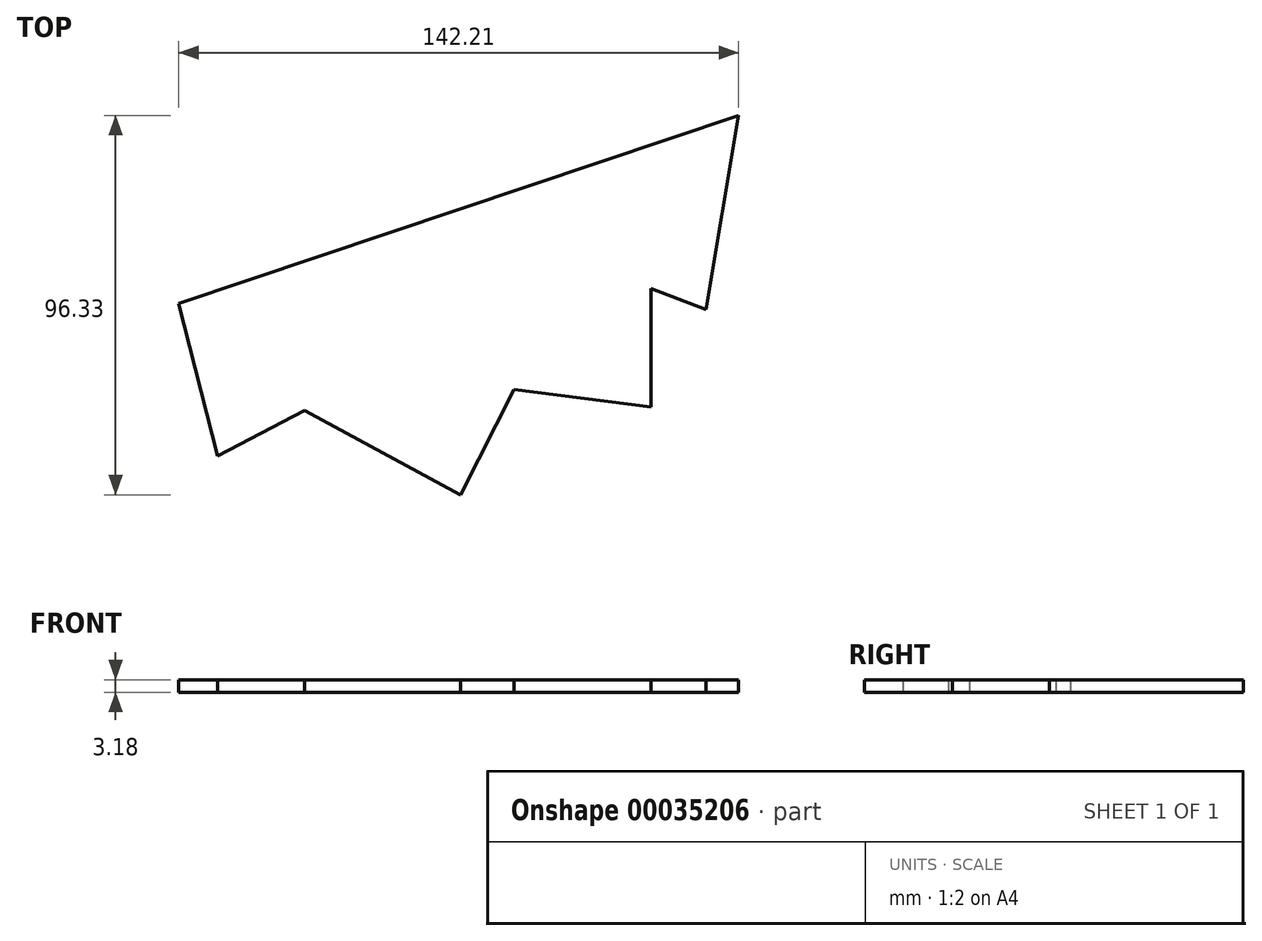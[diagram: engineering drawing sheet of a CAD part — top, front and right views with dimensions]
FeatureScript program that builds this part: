
annotation { "Feature Type Name" : "Feature", "Feature Type Description" : "" }
export const myFeature = defineFeature(function(context is Context, id is Id, definition is map)
    precondition{}
    {
        {
            var Q0;
            Q0=qCreatedBy(makeId("Top.planeOp"),FACE);
            var sketch = newSketch(context, id + "F0", { "sketchPlane" : qUnion([Q0])});
            skLineSegment(sketch, "E0", {"start": v(-83.48, 20.34) * mm, "end": v(58.73, 68.04) * mm});
            skLineSegment(sketch, "E1", {"start": v(58.73, 68.04) * mm, "end": v(50.52, 18.72) * mm});
            skLineSegment(sketch, "E2", {"start": v(50.52, 18.72) * mm, "end": v(36.5, 24.06) * mm});
            skLineSegment(sketch, "E3", {"start": v(36.5, 24.06) * mm, "end": v(36.5, -5.94) * mm});
            skLineSegment(sketch, "E4", {"start": v(36.5, -5.94) * mm, "end": v(1.78, -1.56) * mm});
            skLineSegment(sketch, "E5", {"start": v(1.78, -1.56) * mm, "end": v(-11.85, -28.29) * mm});
            skLineSegment(sketch, "E6", {"start": v(-11.85, -28.29) * mm, "end": v(-51.44, -6.9) * mm});
            skLineSegment(sketch, "E7", {"start": v(-51.44, -6.9) * mm, "end": v(-73.62, -18.43) * mm});
            skLineSegment(sketch, "E8", {"start": v(-73.62, -18.43) * mm, "end": v(-83.48, 20.34) * mm});
            skSolve(sketch);
        }
        {
            var Q0;
            Q0=makeQuery(id+"F0.imprint","IMPRINT",FACE,{"disambiguationData":[TD([[makeQuery(id+"F0.imprint","IMPRINT",EDGE,{"derivedFrom":sQuery(id+"F0.wireOp",EDGE,"E0")}),-1.0]])]});
            extrude(context, id + "F1", {"entities" : qUnion([Q0]), "depth" : 3.18 * mm});
        }
    });
